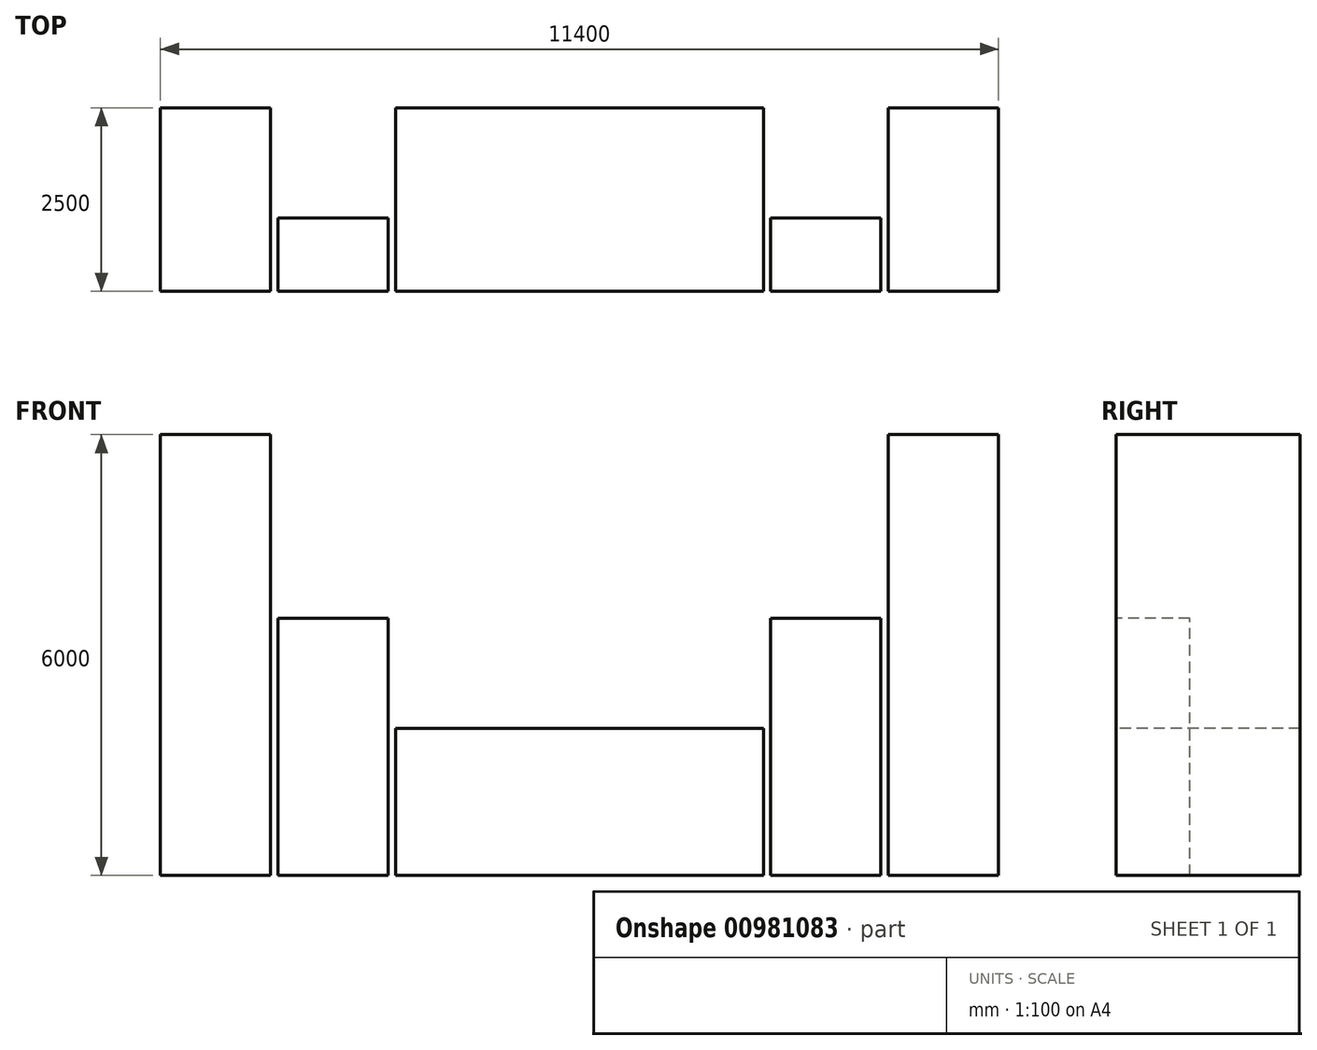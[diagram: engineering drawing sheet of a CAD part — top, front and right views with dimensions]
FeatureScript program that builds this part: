
annotation { "Feature Type Name" : "Feature", "Feature Type Description" : "" }
export const myFeature = defineFeature(function(context is Context, id is Id, definition is map)
    precondition{}
    {
        {
            var Q0;
            Q0=qCreatedBy(makeId("Front.planeOp"),FACE);
            var sketch = newSketch(context, id + "F0", { "sketchPlane" : qUnion([Q0])});
            skLineSegment(sketch, "E0.bottom", {"start": v(-74.59, 0) * mm, "end": v(4925.41, 0) * mm});
            skLineSegment(sketch, "E0.top", {"start": v(-74.59, -2000) * mm, "end": v(4925.41, -2000) * mm});
            skLineSegment(sketch, "E0.left", {"start": v(-74.59, 0) * mm, "end": v(-74.59, -2000) * mm});
            skLineSegment(sketch, "E0.right", {"start": v(4925.41, 0) * mm, "end": v(4925.41, -2000) * mm});
            skSolve(sketch);
        }
        {
            var Q0;
            Q0=qCreatedBy(makeId("Front.planeOp"),FACE);
            var sketch = newSketch(context, id + "F1", { "sketchPlane" : qUnion([Q0])});
            skLineSegment(sketch, "E1.0.0", {"start": v(-74.59, 0) * mm, "end": v(-74.59, -2000) * mm});
            skLineSegment(sketch, "E1.0.1", {"start": v(-74.59, -2000) * mm, "end": v(4925.41, -2000) * mm});
            skLineSegment(sketch, "E1.0.2", {"start": v(4925.41, -2000) * mm, "end": v(4925.41, 0) * mm});
            skLineSegment(sketch, "E1.0.3", {"start": v(4925.41, 0) * mm, "end": v(-74.59, 0) * mm});
            skLineSegment(sketch, "E2.bottom", {"start": v(-74.59, -2000) * mm, "end": v(-174.59, -2000) * mm, "construction": true});
            skLineSegment(sketch, "E2.top", {"start": v(-74.59, 0) * mm, "end": v(-174.59, 0) * mm, "construction": true});
            skLineSegment(sketch, "E2.left", {"start": v(-74.59, -2000) * mm, "end": v(-74.59, 0) * mm, "construction": true});
            skLineSegment(sketch, "E2.right", {"start": v(-174.59, -2000) * mm, "end": v(-174.59, 0) * mm, "construction": true});
            skLineSegment(sketch, "E3.bottom", {"start": v(4925.41, -2000) * mm, "end": v(5025.41, -2000) * mm, "construction": true});
            skLineSegment(sketch, "E3.top", {"start": v(4925.41, 0) * mm, "end": v(5025.41, 0) * mm, "construction": true});
            skLineSegment(sketch, "E3.left", {"start": v(4925.41, -2000) * mm, "end": v(4925.41, 0) * mm, "construction": true});
            skLineSegment(sketch, "E3.right", {"start": v(5025.41, -2000) * mm, "end": v(5025.41, 0) * mm, "construction": true});
            skLineSegment(sketch, "E4.bottom", {"start": v(-174.59, -2000) * mm, "end": v(-1674.59, -2000) * mm});
            skLineSegment(sketch, "E4.top", {"start": v(-174.59, 1500) * mm, "end": v(-1674.59, 1500) * mm});
            skLineSegment(sketch, "E4.left", {"start": v(-174.59, -2000) * mm, "end": v(-174.59, 1500) * mm});
            skLineSegment(sketch, "E4.right", {"start": v(-1674.59, -2000) * mm, "end": v(-1674.59, 1500) * mm});
            skLineSegment(sketch, "E5.bottom", {"start": v(5025.41, -2000) * mm, "end": v(6525.41, -2000) * mm});
            skLineSegment(sketch, "E5.top", {"start": v(5025.41, 1500) * mm, "end": v(6525.41, 1500) * mm});
            skLineSegment(sketch, "E5.left", {"start": v(5025.41, -2000) * mm, "end": v(5025.41, 1500) * mm});
            skLineSegment(sketch, "E5.right", {"start": v(6525.41, -2000) * mm, "end": v(6525.41, 1500) * mm});
            skSolve(sketch);
        }
        {
            var Q0;
            Q0=qCreatedBy(makeId("Front.planeOp"),FACE);
            var sketch = newSketch(context, id + "F2", { "sketchPlane" : qUnion([Q0])});
            skLineSegment(sketch, "E6.0.0", {"start": v(-174.59, -2000) * mm, "end": v(-174.59, 1500) * mm});
            skLineSegment(sketch, "E6.0.1", {"start": v(-174.59, 1500) * mm, "end": v(-1674.59, 1500) * mm});
            skLineSegment(sketch, "E6.0.2", {"start": v(-1674.59, 1500) * mm, "end": v(-1674.59, -2000) * mm});
            skLineSegment(sketch, "E6.0.3", {"start": v(-1674.59, -2000) * mm, "end": v(-174.59, -2000) * mm});
            skLineSegment(sketch, "E7.0.0", {"start": v(6525.41, 1500) * mm, "end": v(5025.41, 1500) * mm});
            skLineSegment(sketch, "E7.0.1", {"start": v(5025.41, 1500) * mm, "end": v(5025.41, -2000) * mm});
            skLineSegment(sketch, "E7.0.2", {"start": v(5025.41, -2000) * mm, "end": v(6525.41, -2000) * mm});
            skLineSegment(sketch, "E7.0.3", {"start": v(6525.41, -2000) * mm, "end": v(6525.41, 1500) * mm});
            skLineSegment(sketch, "E8.bottom", {"start": v(-1674.59, -2000) * mm, "end": v(-1774.59, -2000) * mm, "construction": true});
            skLineSegment(sketch, "E8.top", {"start": v(-1674.59, 1000) * mm, "end": v(-1774.59, 1000) * mm, "construction": true});
            skLineSegment(sketch, "E8.left", {"start": v(-1674.59, -2000) * mm, "end": v(-1674.59, 1000) * mm, "construction": true});
            skLineSegment(sketch, "E8.right", {"start": v(-1774.59, -2000) * mm, "end": v(-1774.59, 1000) * mm, "construction": true});
            skLineSegment(sketch, "E9.bottom", {"start": v(6525.41, 1500) * mm, "end": v(6625.41, 1500) * mm, "construction": true});
            skLineSegment(sketch, "E9.top", {"start": v(6525.41, -2000) * mm, "end": v(6625.41, -2000) * mm, "construction": true});
            skLineSegment(sketch, "E9.left", {"start": v(6525.41, 1500) * mm, "end": v(6525.41, -2000) * mm, "construction": true});
            skLineSegment(sketch, "E9.right", {"start": v(6625.41, 1500) * mm, "end": v(6625.41, -2000) * mm, "construction": true});
            skLineSegment(sketch, "E10.bottom", {"start": v(-1774.59, -2000) * mm, "end": v(-3274.59, -2000) * mm});
            skLineSegment(sketch, "E10.top", {"start": v(-1774.59, 4000) * mm, "end": v(-3274.59, 4000) * mm});
            skLineSegment(sketch, "E10.left", {"start": v(-1774.59, -2000) * mm, "end": v(-1774.59, 4000) * mm});
            skLineSegment(sketch, "E10.right", {"start": v(-3274.59, -2000) * mm, "end": v(-3274.59, 4000) * mm});
            skLineSegment(sketch, "E11.bottom", {"start": v(6625.41, -2000) * mm, "end": v(8125.41, -2000) * mm});
            skLineSegment(sketch, "E11.top", {"start": v(6625.41, 4000) * mm, "end": v(8125.41, 4000) * mm});
            skLineSegment(sketch, "E11.left", {"start": v(6625.41, -2000) * mm, "end": v(6625.41, 4000) * mm});
            skLineSegment(sketch, "E11.right", {"start": v(8125.41, -2000) * mm, "end": v(8125.41, 4000) * mm});
            skSolve(sketch);
        }
        {
            var Q0;
            Q0 = qSketchRegion(id + "F0", true);
            extrude(context, id + "F3", {"entities" : qUnion([Q0]), "oppositeDirection" : true, "depth" : 2500 * mm, "offsetDistance" : 25 * mm});
        }
        {
            var Q0;
            Q0=makeQuery(id+"F2.imprint","IMPRINT",FACE,{"disambiguationData":[TD([[makeQuery(id+"F2.imprint","IMPRINT",EDGE,{"derivedFrom":sQuery(id+"F2.wireOp",EDGE,"E6.0.0")}),1.0]])]});
            var Q1;
            Q1=makeQuery(id+"F2.imprint","IMPRINT",FACE,{"disambiguationData":[TD([[makeQuery(id+"F2.imprint","IMPRINT",EDGE,{"derivedFrom":sQuery(id+"F2.wireOp",EDGE,"E7.0.0")}),1.0]])]});
            extrude(context, id + "F4", {"entities" : qUnion([Q0, Q1]), "oppositeDirection" : true, "depth" : 1000 * mm, "offsetDistance" : 25 * mm});
        }
        {
            var Q0;
            Q0=makeQuery(id+"F2.imprint","IMPRINT",FACE,{"disambiguationData":[TD([[makeQuery(id+"F2.imprint","IMPRINT",EDGE,{"derivedFrom":sQuery(id+"F2.wireOp",EDGE,"E10.bottom")}),-1.0]])]});
            var Q1;
            Q1=makeQuery(id+"F2.imprint","IMPRINT",FACE,{"disambiguationData":[TD([[makeQuery(id+"F2.imprint","IMPRINT",EDGE,{"derivedFrom":sQuery(id+"F2.wireOp",EDGE,"E11.bottom")}),1.0]])]});
            extrude(context, id + "F5", {"entities" : qUnion([Q0, Q1]), "oppositeDirection" : true, "depth" : 2500 * mm, "offsetDistance" : 25 * mm});
        }
    });
